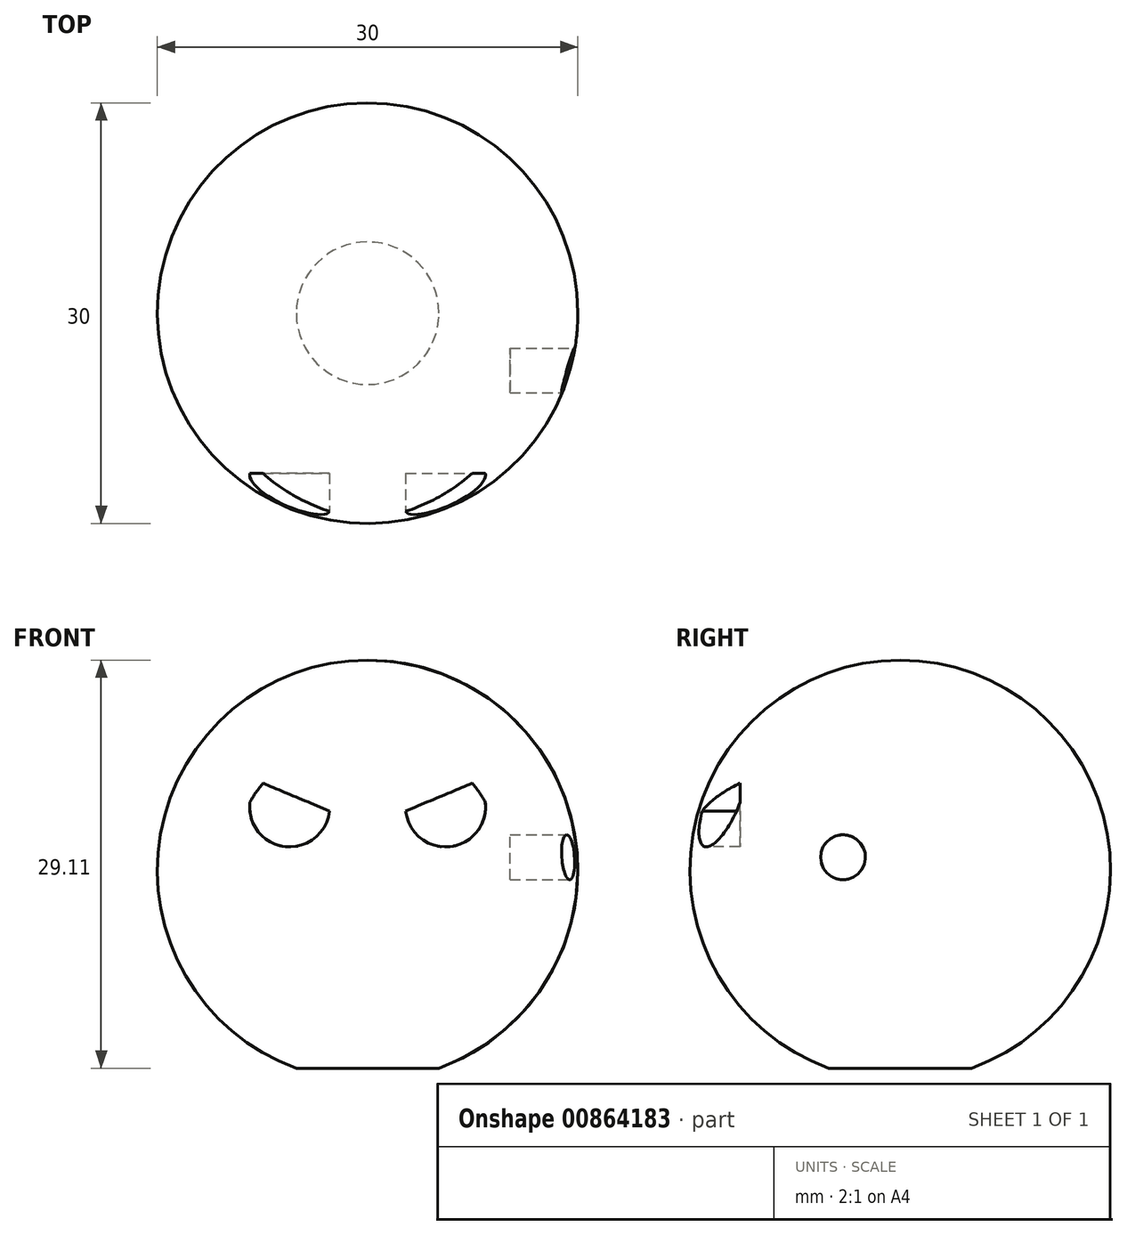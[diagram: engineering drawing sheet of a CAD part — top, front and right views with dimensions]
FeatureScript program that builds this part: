
annotation { "Feature Type Name" : "Feature", "Feature Type Description" : "" }
export const myFeature = defineFeature(function(context is Context, id is Id, definition is map)
    precondition{}
    {
        {
            var Q0;
            Q0=qCreatedBy(makeId("Front.planeOp"),FACE);
            var sketch = newSketch(context, id + "F0", { "sketchPlane" : qUnion([Q0])});
            skLineSegment(sketch, "E0", {"start": v(0, 0) * mm, "end": v(0, 30) * mm});
            skArc(sketch, "E1", {"start": v(0, 0) * mm, "mid": v(15, 15) * mm, "end": v(0, 30) * mm});
            skSolve(sketch);
        }
        {
            var Q0;
            Q0=makeQuery(id+"F0.imprint","IMPRINT",FACE,{"disambiguationData":[TD([[makeQuery(id+"F0.imprint","IMPRINT",EDGE,{"derivedFrom":sQuery(id+"F0.wireOp",EDGE,"E0")}),-1.0]])]});
            var Q1;
            Q1=sQuery(id+"F0.wireOp",EDGE,"E0");
            revolve(context, id + "F1", {"surfaceOperationType" : NewSurfaceOperationType.NEW, "entities" : qUnion([Q0]), "axis" : qUnion([Q1]), "revolveType" : RevolveType.FULL});
        }
        {
            var Q0;
            Q0=qCreatedBy(makeId("Front.planeOp"),FACE);
            cPlane(context, id + "F2", {"entities" : qUnion([Q0]), "cplaneType" : CPlaneType.OFFSET, "offset" : 25.4 * mm, "width" : 152.4 * mm, "height" : 152.4 * mm});
        }
        {
            var Q0;
            Q0=qCreatedBy(makeId("Right.planeOp"),FACE);
            cPlane(context, id + "F3", {"entities" : qUnion([Q0]), "cplaneType" : CPlaneType.OFFSET, "offset" : 25.4 * mm, "width" : 152.4 * mm, "height" : 152.4 * mm});
        }
        {
            var Q0;
            Q0=qCreatedBy(id+"F2.planeOp",FACE);
            var sketch = newSketch(context, id + "F4", { "sketchPlane" : qUnion([Q0])});
            skLineSegment(sketch, "E2", {"start": v(-2.72, 19.24) * mm, "end": v(-7.78, 21.34) * mm});
            skArc(sketch, "E3", {"start": v(-7.78, 21.34) * mm, "mid": v(-6.66, 16.9) * mm, "end": v(-2.72, 19.24) * mm});
            skLineSegment(sketch, "E4.MirrorCS", {"start": v(2.72, 19.24) * mm, "end": v(7.78, 21.34) * mm});
            skArc(sketch, "E5.MirrorCS", {"start": v(7.78, 21.34) * mm, "mid": v(6.66, 16.9) * mm, "end": v(2.72, 19.24) * mm});
            skSolve(sketch);
        }
        {
            var Q0;
            Q0=makeQuery(id+"F4.imprint","IMPRINT",FACE,{"disambiguationData":[TD([[makeQuery(id+"F4.imprint","IMPRINT",EDGE,{"derivedFrom":sQuery(id+"F4.wireOp",EDGE,"E2")}),1.0]])]});
            var Q1;
            Q1=makeQuery(id+"F4.imprint","IMPRINT",FACE,{"disambiguationData":[TD([[makeQuery(id+"F4.imprint","IMPRINT",EDGE,{"derivedFrom":sQuery(id+"F4.wireOp",EDGE,"E4.MirrorCS")}),-1.0]])]});
            extrude(context, id + "F5", {"entities" : qUnion([Q0, Q1]), "operationType" : NewBodyOperationType.REMOVE, "oppositeDirection" : true, "depth" : 13.97 * mm, "offsetDistance" : 25.4 * mm});
        }
        {
            var Q0;
            Q0=qCreatedBy(id+"F3.planeOp",FACE);
            var sketch = newSketch(context, id + "F6", { "sketchPlane" : qUnion([Q0])});
            skCircle(sketch, "E6", {"center": v(-4.09, 15.94) * mm, "radius": 1.6 * mm});
            skSolve(sketch);
        }
        {
            var Q0;
            Q0=makeQuery(id+"F6.imprint","IMPRINT",FACE,{"disambiguationData":[TD([[makeQuery(id+"F6.imprint","IMPRINT",EDGE,{"derivedFrom":sQuery(id+"F6.wireOp",EDGE,"E6")}),1.0]])]});
            extrude(context, id + "F7", {"entities" : qUnion([Q0]), "operationType" : NewBodyOperationType.REMOVE, "oppositeDirection" : true, "depth" : 15.24 * mm, "offsetDistance" : 25.4 * mm});
        }
        {
            var Q0;
            Q0=qCreatedBy(id+"F2.planeOp",FACE);
            var sketch = newSketch(context, id + "F8", { "sketchPlane" : qUnion([Q0])});
            skLineSegment(sketch, "E7.bottom", {"start": v(-16.84, 0.89) * mm, "end": v(19.29, 0.89) * mm});
            skLineSegment(sketch, "E7.top", {"start": v(-16.84, -8.9) * mm, "end": v(19.29, -8.9) * mm});
            skLineSegment(sketch, "E7.left", {"start": v(-16.84, 0.89) * mm, "end": v(-16.84, -8.9) * mm});
            skLineSegment(sketch, "E7.right", {"start": v(19.29, 0.89) * mm, "end": v(19.29, -8.9) * mm});
            skSolve(sketch);
        }
        {
            var Q0;
            Q0=makeQuery(id+"F8.imprint","IMPRINT",FACE,{"disambiguationData":[TD([[makeQuery(id+"F8.imprint","IMPRINT",EDGE,{"derivedFrom":sQuery(id+"F8.wireOp",EDGE,"E7.bottom")}),-1.0]])]});
            extrude(context, id + "F9", {"entities" : qUnion([Q0]), "operationType" : NewBodyOperationType.REMOVE, "oppositeDirection" : true, "depth" : 76.2 * mm, "offsetDistance" : 25.4 * mm});
        }
    });
